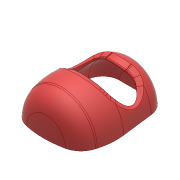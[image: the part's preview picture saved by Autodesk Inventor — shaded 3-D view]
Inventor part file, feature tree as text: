
AUTODESK INVENTOR PART (.ipt)
format: ipt  version: 2017 (Build 210142000, 142)  size: 553,472 bytes
history: native  units: mm
features: fillet x3, chamfer x3, sketch x3, extrude x2, revolve x1, shell x1
ambient origin geometry x8: Origin, YZ Plane, XZ Plane, XY Plane, X Axis, Y Axis, Z Axis, Center Point
bodies: Solid1 (feature_tree)
feature tree (13):
  revolve  "Revolution1"  [1 undecoded]
  fillet  "Fillet1"  Radius=30.0mm
  chamfer  "Chamfer1"  Distance=10.0mm Angle=45.0deg
  fillet  "Fillet2"  Radius=20.0mm
  fillet  "Fillet3"  Radius=60.0mm
  extrude  "Extrusion1"  Depth=10.0mm TaperAngle=0.0deg
  shell  "Shell1"  Thickness=4.0mm
  extrude  "Extrusion2"  Depth=28.0mm
  chamfer  "Chamfer2"  Distance=28.0mm
  chamfer  "Chamfer3"  Distance=28.0mm
  sketch  "Sketch1"  dims[d0=40.0mm d1=80.0mm d2=30.0mm]
  sketch  "Sketch2"  dims[d3=90.0deg]
  sketch  "Sketch3"  dims[d4=20.0mm d5=10.0mm d6=20.0mm d7=45.0deg d8=20.0mm d9=60.0mm d10=10.0mm d11=0.0mm d12=4.0mm d13=28.0mm d14=28.0mm d15=28.0mm d16=46.0mm d17=13.0mm d18=100.0mm d19=0.0mm d20=80.0mm d21=10.0mm d22=0.0mm d24=120.0mm d25=80.0mm d26=3.0mm d27=2.0mm d28=45.0deg d29=3.0mm d30=2.0mm d31=45.0deg]
note: 1 required parameter value undecoded (feature->parameter linkage not recoverable at this tier; creation-order binding heuristic only, values carry confidence <= 0.55)
